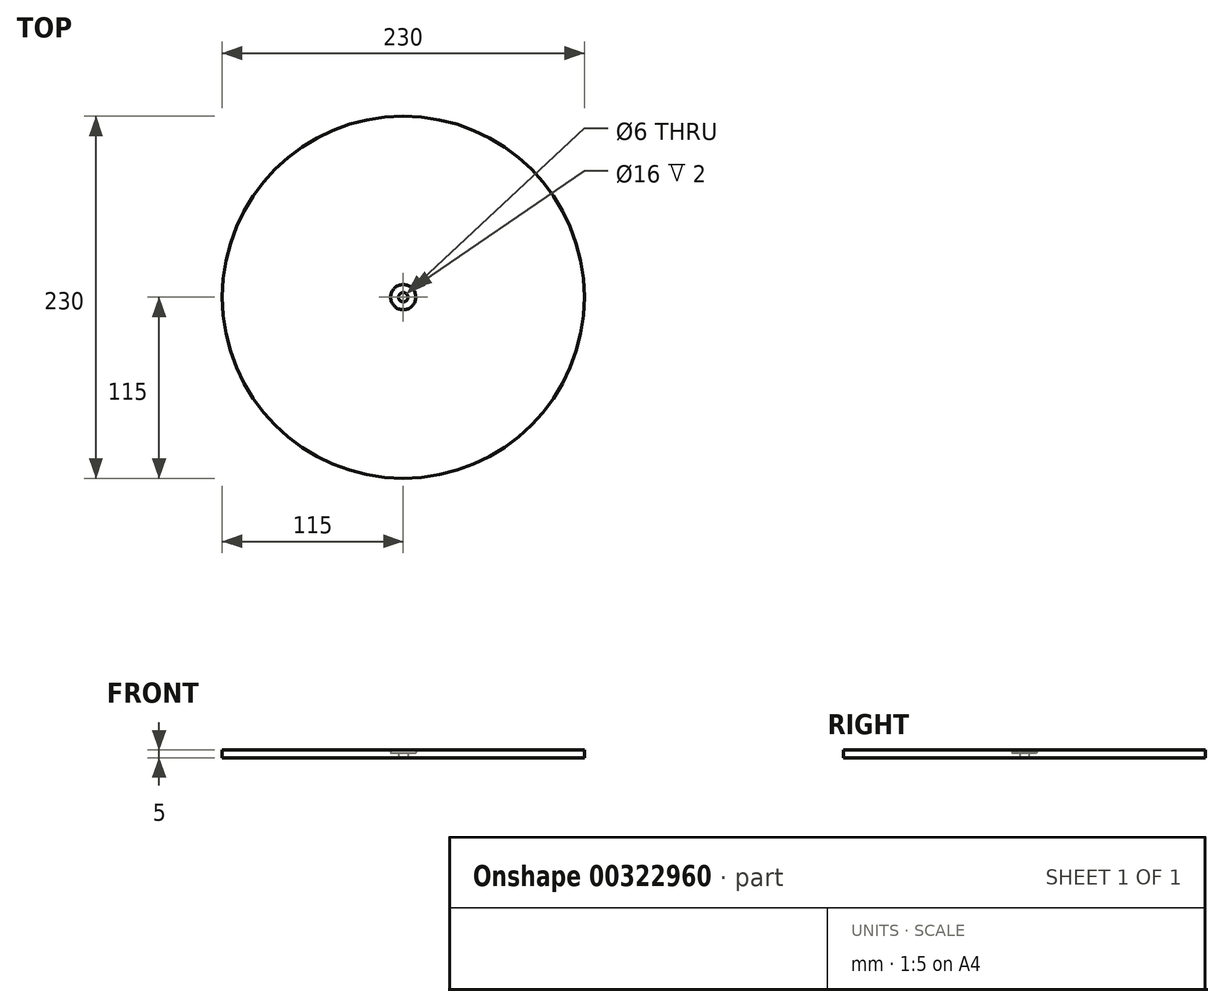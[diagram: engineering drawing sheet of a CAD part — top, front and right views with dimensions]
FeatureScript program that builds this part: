
annotation { "Feature Type Name" : "Feature", "Feature Type Description" : "" }
export const myFeature = defineFeature(function(context is Context, id is Id, definition is map)
    precondition{}
    {
        {
            var Q0;
            Q0=qCreatedBy(makeId("Front.planeOp"),FACE);
            var sketch = newSketch(context, id + "F0", { "sketchPlane" : qUnion([Q0])});
            skLineSegment(sketch, "E0", {"start": v(0, 0) * mm, "end": v(-3, 0) * mm, "construction": true});
            skLineSegment(sketch, "E1", {"start": v(-3, 0) * mm, "end": v(-3, 3) * mm});
            skLineSegment(sketch, "E2", {"start": v(-3, 3) * mm, "end": v(-8, 3) * mm});
            skLineSegment(sketch, "E3", {"start": v(-8, 3) * mm, "end": v(-8, 5) * mm});
            skLineSegment(sketch, "E4", {"start": v(-8, 5) * mm, "end": v(-115, 5) * mm});
            skLineSegment(sketch, "E5", {"start": v(-115, 5) * mm, "end": v(-115, 0) * mm});
            skLineSegment(sketch, "E6", {"start": v(-115, 0) * mm, "end": v(-3, 0) * mm});
            skLineSegment(sketch, "E7", {"start": v(0, -4.69) * mm, "end": v(0, 21.47) * mm, "construction": true});
            skSolve(sketch);
        }
        {
            var Q0;
            Q0 = qSketchRegion(id + "F0", true);
            var Q1;
            Q1=sQuery(id+"F0.wireOp",EDGE,"E7");
            revolve(context, id + "F1", {"entities" : qUnion([Q0]), "axis" : qUnion([Q1]), "revolveType" : RevolveType.FULL});
        }
    });
